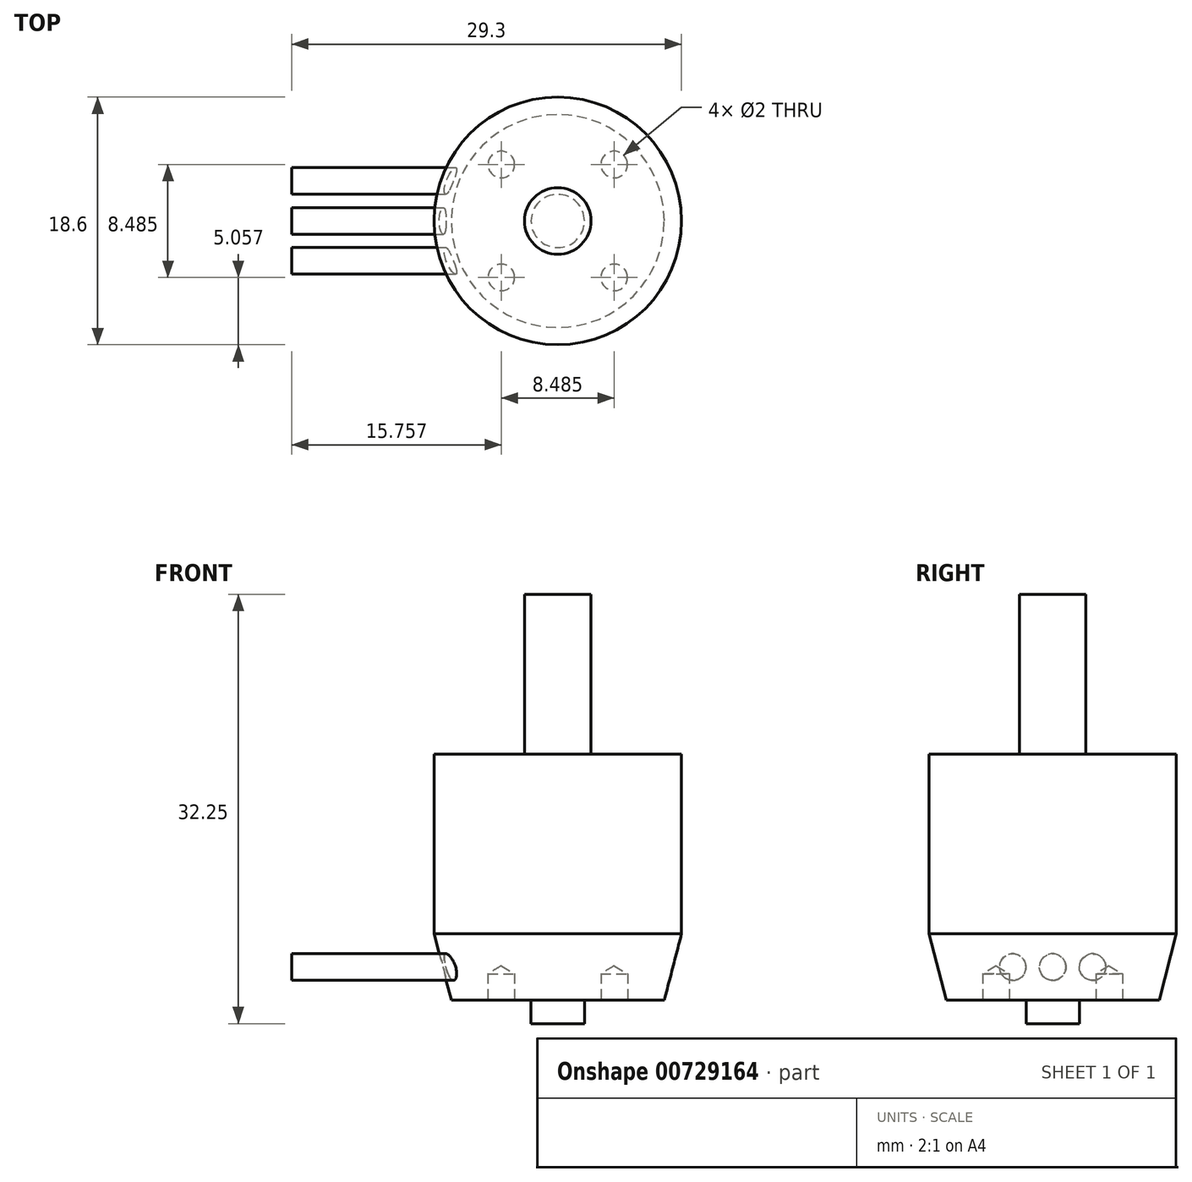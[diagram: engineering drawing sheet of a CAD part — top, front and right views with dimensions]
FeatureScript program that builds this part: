
annotation { "Feature Type Name" : "Feature", "Feature Type Description" : "" }
export const myFeature = defineFeature(function(context is Context, id is Id, definition is map)
    precondition{}
    {
        {
            var Q0;
            Q0=qCreatedBy(makeId("Top.planeOp"),FACE);
            var sketch = newSketch(context, id + "F0", { "sketchPlane" : qUnion([Q0])});
            skCircle(sketch, "E0", {"center": v(0, 0) * mm, "radius": 9.3 * mm});
            skSolve(sketch);
        }
        {
            var Q0;
            Q0=qCreatedBy(makeId("Top.planeOp"),FACE);
            var sketch = newSketch(context, id + "F1", { "sketchPlane" : qUnion([Q0])});
            skCircle(sketch, "E1", {"center": v(0, 0) * mm, "radius": 6 * mm, "construction": true});
            skLineSegment(sketch, "E2", {"start": v(0, 0) * mm, "end": v(-4.24, 4.24) * mm, "construction": true});
            skCircle(sketch, "E3", {"center": v(-4.24, 4.24) * mm, "radius": 1 * mm});
            skCircle(sketch, "E4.1.0", {"center": v(-4.24, -4.24) * mm, "radius": 1 * mm});
            skCircle(sketch, "E4.2.0", {"center": v(4.24, -4.24) * mm, "radius": 1 * mm});
            skCircle(sketch, "E4.3.0", {"center": v(4.24, 4.24) * mm, "radius": 1 * mm});
            skSolve(sketch);
        }
        {
            var Q0;
            Q0=qCreatedBy(makeId("Top.planeOp"),FACE);
            var sketch = newSketch(context, id + "F2", { "sketchPlane" : qUnion([Q0])});
            skCircle(sketch, "E5", {"center": v(0, 0) * mm, "radius": 2.5 * mm});
            skSolve(sketch);
        }
        {
            var Q0;
            Q0=qCreatedBy(makeId("Top.planeOp"),FACE);
            var sketch = newSketch(context, id + "F3", { "sketchPlane" : qUnion([Q0])});
            skCircle(sketch, "E6", {"center": v(0, 0) * mm, "radius": 2 * mm});
            skSolve(sketch);
        }
        {
            var Q0;
            Q0 = qSketchRegion(id + "F0", true);
            extrude(context, id + "F4", {"entities" : qUnion([Q0]), "depth" : 18.5 * mm, "offsetDistance" : 25 * mm});
        }
        {
            var Q0;
            Q0 = qSketchRegion(id + "F2", true);
            extrude(context, id + "F5", {"entities" : qUnion([Q0]), "operationType" : NewBodyOperationType.ADD, "depth" : 30.5 * mm, "offsetDistance" : 25 * mm});
        }
        {
            var Q0;
            Q0=makeQuery(id+"F3.imprint","IMPRINT",FACE,{"disambiguationData":[TD([[makeQuery(id+"F3.imprint","IMPRINT",EDGE,{"derivedFrom":sQuery(id+"F3.wireOp",EDGE,"E6")}),1.0]])]});
            extrude(context, id + "F6", {"entities" : qUnion([Q0]), "operationType" : NewBodyOperationType.ADD, "oppositeDirection" : true, "depth" : 1.75 * mm, "offsetDistance" : 25 * mm});
        }
        {
            var Q0;
            Q0=makeQuery(id+"F4.opExtrude","CAP_EDGE",EDGE,{"disambiguationData":[OSD([sQuery(id+"F0.wireOp",EDGE,"E0")])],"isStart":true});
            chamfer(context, id + "F7", {"entities" : qUnion([Q0]), "chamferType" : ChamferType.TWO_OFFSETS, "width1" : 5 * mm, "oppositeDirection" : false, "width2" : 1.3 * mm, "tangentPropagation" : true});
        }
        {
            var Q0;
            Q0=qCreatedBy(makeId("Right.planeOp"),FACE);
            var sketch = newSketch(context, id + "F8", { "sketchPlane" : qUnion([Q0])});
            skCircle(sketch, "E7", {"center": v(0, 2.5) * mm, "radius": 1 * mm});
            skCircle(sketch, "E8", {"center": v(-3, 2.5) * mm, "radius": 1 * mm});
            skCircle(sketch, "E9", {"center": v(3, 2.5) * mm, "radius": 1 * mm});
            skLineSegment(sketch, "E10", {"start": v(3, 2.5) * mm, "end": v(-3, 2.5) * mm, "construction": true});
            skSolve(sketch);
        }
        {
            var Q0;
            Q0 = qSketchRegion(id + "F8", true);
            extrude(context, id + "F9", {"entities" : qUnion([Q0]), "operationType" : NewBodyOperationType.ADD, "oppositeDirection" : true, "depth" : 20 * mm, "offsetDistance" : 25 * mm});
        }
        {
            var Q0;
            Q0=sQuery(id+"F1.wireOp",VERTEX,"E3.center");
            var Q1;
            Q1=sQuery(id+"F1.wireOp",VERTEX,"E4.1.0.center");
            var Q2;
            Q2=sQuery(id+"F1.wireOp",VERTEX,"E4.2.0.center");
            var Q3;
            Q3=sQuery(id+"F1.wireOp",VERTEX,"E4.3.0.center");
            var Q4;
            Q4=makeQuery(id+"F4.opExtrude","SWEPT_BODY",BODY,{"disambiguationData":[OSD([sQuery(id+"F0.wireOp",EDGE,"E0")])]});
            hole(context, id + "F10", {"style" : HoleStyle.SIMPLE, "endStyle" : HoleEndStyle.BLIND, "oppositeDirection" : true, "holeDiameter" : 2 * mm, "majorDiameter" : 5 * mm, "holeDepth" : 2 * mm, "isTappedThrough" : true, "tappedDepth" : 12 * mm, "tapClearance" : 3, "locations" : qUnion([Q0, Q1, Q2, Q3]), "scope" : qUnion([Q4])});
        }
    });
